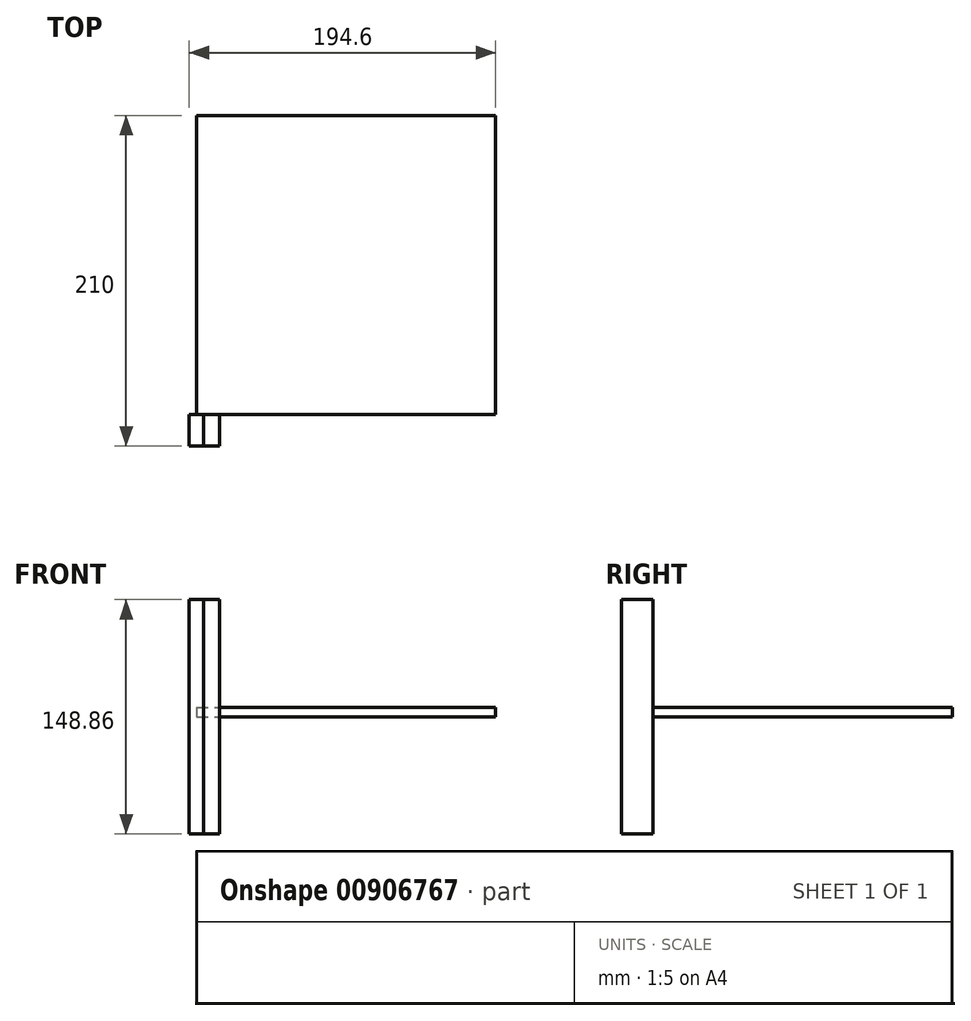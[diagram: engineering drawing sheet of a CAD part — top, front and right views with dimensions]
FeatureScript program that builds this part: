
annotation { "Feature Type Name" : "Feature", "Feature Type Description" : "" }
export const myFeature = defineFeature(function(context is Context, id is Id, definition is map)
    precondition{}
    {
        {
            var Q0;
            Q0=qCreatedBy(makeId("Top.planeOp"),FACE);
            var sketch = newSketch(context, id + "F0", { "sketchPlane" : qUnion([Q0])});
            skLineSegment(sketch, "E0.bottom", {"start": v(0, 0) * mm, "end": v(190, 0) * mm});
            skLineSegment(sketch, "E0.top", {"start": v(0, 190) * mm, "end": v(190, 190) * mm});
            skLineSegment(sketch, "E0.left", {"start": v(0, 0) * mm, "end": v(0, 190) * mm});
            skLineSegment(sketch, "E0.right", {"start": v(190, 0) * mm, "end": v(190, 190) * mm});
            skSolve(sketch);
        }
        {
            var Q0;
            Q0=makeQuery(id+"F0.imprint","IMPRINT",FACE,{"disambiguationData":[TD([[makeQuery(id+"F0.imprint","IMPRINT",EDGE,{"derivedFrom":sQuery(id+"F0.wireOp",EDGE,"E0.bottom")}),1.0]])]});
            extrude(context, id + "F1", {"entities" : qUnion([Q0]), "depth" : 6 * mm, "offsetDistance" : 25 * mm});
        }
        {
            var Q0;
            Q0=qCreatedBy(makeId("Front.planeOp"),FACE);
            var sketch = newSketch(context, id + "F2", { "sketchPlane" : qUnion([Q0])});
            skLineSegment(sketch, "E1.bottom", {"start": v(-4.6, 74.43) * mm, "end": v(4.6, 74.43) * mm});
            skLineSegment(sketch, "E1.top", {"start": v(-4.6, -74.43) * mm, "end": v(4.6, -74.43) * mm});
            skLineSegment(sketch, "E1.left", {"start": v(-4.6, 74.43) * mm, "end": v(-4.6, -74.43) * mm});
            skLineSegment(sketch, "E1.right", {"start": v(4.6, 74.43) * mm, "end": v(4.6, -74.43) * mm});
            skPoint(sketch, "E1.middle", {"position": v(0, 0) * mm});
            skSolve(sketch);
        }
        {
            var Q0;
            Q0=makeQuery(id+"F2.imprint","IMPRINT",FACE,{"disambiguationData":[TD([[makeQuery(id+"F2.imprint","IMPRINT",EDGE,{"derivedFrom":sQuery(id+"F2.wireOp",EDGE,"E1.bottom")}),-1.0]])]});
            extrude(context, id + "F3", {"entities" : qUnion([Q0]), "depth" : 20 * mm, "offsetDistance" : 25 * mm});
        }
        {
            var Q0;
            Q0=makeQuery(id+"F3.opExtrude","SWEPT_FACE",FACE,{"disambiguationData":[OSD([sQuery(id+"F2.wireOp",EDGE,"E1.right")])]});
            extrude(context, id + "F4", {"entities" : qUnion([Q0]), "depth" : 10 * mm, "offsetDistance" : 25 * mm});
        }
    });
